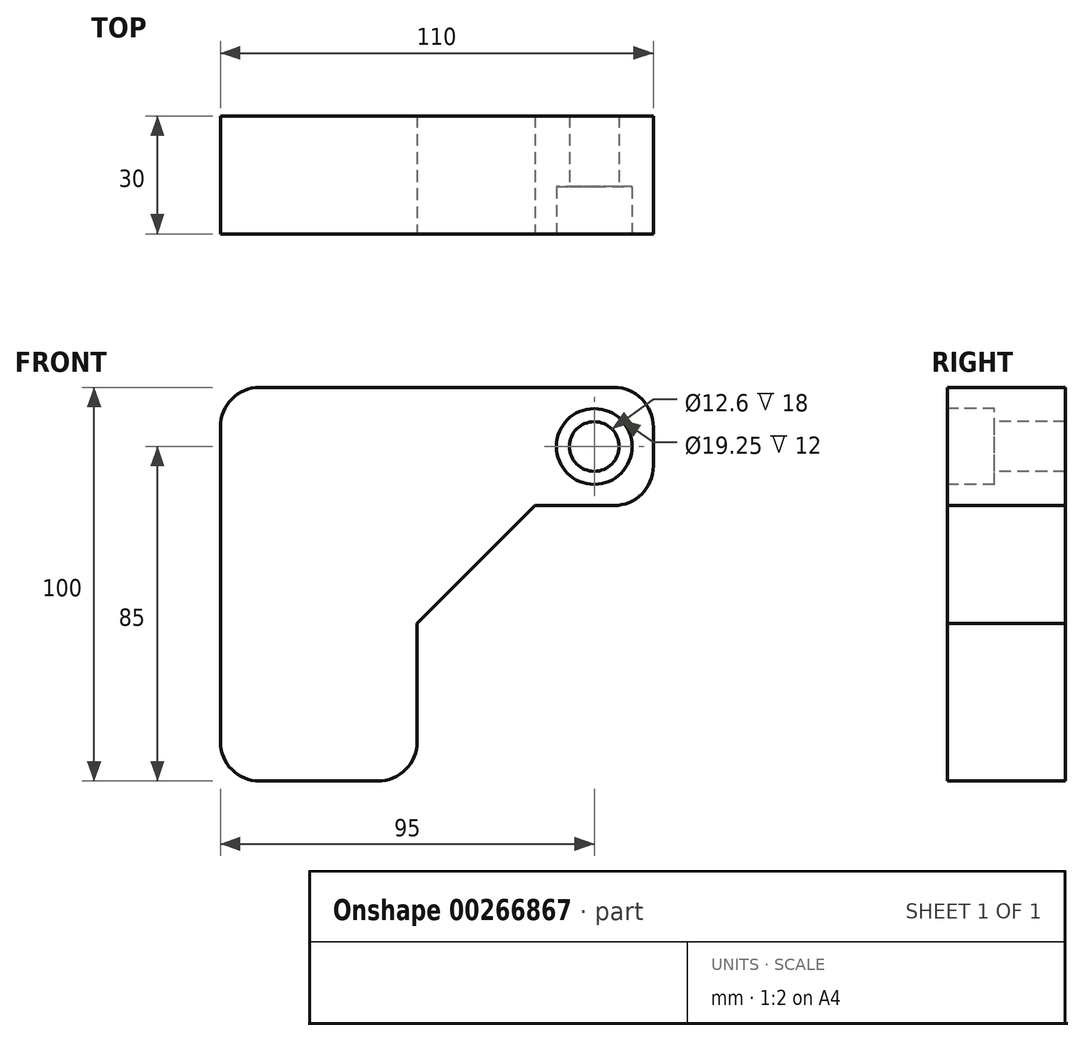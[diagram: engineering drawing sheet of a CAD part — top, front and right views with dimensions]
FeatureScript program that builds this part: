
annotation { "Feature Type Name" : "Feature", "Feature Type Description" : "" }
export const myFeature = defineFeature(function(context is Context, id is Id, definition is map)
    precondition{}
    {
        {
            var Q0;
            Q0=qCreatedBy(makeId("Front.planeOp"),FACE);
            var sketch = newSketch(context, id + "F0", { "sketchPlane" : qUnion([Q0])});
            skLineSegment(sketch, "E0", {"start": v(0, 0) * mm, "end": v(30, 30) * mm});
            skLineSegment(sketch, "E1", {"start": v(60, 60) * mm, "end": v(-50, 60) * mm});
            skLineSegment(sketch, "E2", {"start": v(-50, 60) * mm, "end": v(-50, -40) * mm});
            skLineSegment(sketch, "E3", {"start": v(-50, -40) * mm, "end": v(0, -40) * mm});
            skLineSegment(sketch, "E4", {"start": v(0, -40) * mm, "end": v(0, 0) * mm});
            skLineSegment(sketch, "E5", {"start": v(30, 30) * mm, "end": v(60, 30) * mm});
            skLineSegment(sketch, "E6", {"start": v(60, 30) * mm, "end": v(60, 60) * mm});
            skPoint(sketch, "E7", {"position": v(45, 45) * mm});
            skLineSegment(sketch, "E8", {"start": v(-25, -40) * mm, "end": v(-25, 60) * mm, "construction": true});
            skSolve(sketch);
        }
        {
            var Q0;
            Q0 = qSketchRegion(id + "F0", true);
            extrude(context, id + "F1", {"entities" : qUnion([Q0]), "oppositeDirection" : true, "depth" : 30 * mm});
        }
        {
            var Q0;
            Q0=makeQuery(id+"F1.opExtrude","SWEPT_EDGE",EDGE,{"disambiguationData":[OSD([sQuery(id+"F0.wireOp",EDGE,"E2"),sQuery(id+"F0.wireOp",EDGE,"E3")])]});
            var Q1;
            Q1=makeQuery(id+"F1.opExtrude","SWEPT_EDGE",EDGE,{"disambiguationData":[OSD([sQuery(id+"F0.wireOp",EDGE,"E3"),sQuery(id+"F0.wireOp",EDGE,"E4")])]});
            var Q2;
            Q2=makeQuery(id+"F1.opExtrude","SWEPT_EDGE",EDGE,{"disambiguationData":[OSD([sQuery(id+"F0.wireOp",EDGE,"E1"),sQuery(id+"F0.wireOp",EDGE,"E2")])]});
            var Q3;
            Q3=makeQuery(id+"F1.opExtrude","SWEPT_EDGE",EDGE,{"disambiguationData":[OSD([sQuery(id+"F0.wireOp",EDGE,"E1"),sQuery(id+"F0.wireOp",EDGE,"E6")])]});
            var Q4;
            Q4=makeQuery(id+"F1.opExtrude","SWEPT_EDGE",EDGE,{"disambiguationData":[OSD([sQuery(id+"F0.wireOp",EDGE,"E5"),sQuery(id+"F0.wireOp",EDGE,"E6")])]});
            fillet(context, id + "F2", {"entities" : qUnion([Q0, Q1, Q2, Q3, Q4]), "radius" : 10 * mm, "tangentPropagation" : true, "allowEdgeOverflow" : false});
        }
        {
            var Q0;
            Q0=sQuery(id+"F0.wireOp",VERTEX,"E7");
            var Q1;
            Q1=makeQuery(id+"F1.opExtrude","SWEPT_BODY",BODY,{"disambiguationData":[OSD([sQuery(id+"F0.wireOp",EDGE,"E0"),sQuery(id+"F0.wireOp",EDGE,"E1"),sQuery(id+"F0.wireOp",EDGE,"E2"),sQuery(id+"F0.wireOp",EDGE,"E3"),sQuery(id+"F0.wireOp",EDGE,"E4"),sQuery(id+"F0.wireOp",EDGE,"E5"),sQuery(id+"F0.wireOp",EDGE,"E6")])]});
            hole(context, id + "F3", {"style" : HoleStyle.C_BORE, "endStyle" : HoleEndStyle.THROUGH, "standardTappedOrClearance" : lookupTablePath({ "standard" : "ISO", "fit" : "Close", "size" : "M12", "type" : "Clearance" }), "standardBlindInLast" : lookupTablePath({ "fit" : "Close", "standard" : "ISO", "size" : "M12", "type" : "Clearance" }), "holeDiameter" : 12.6 * mm, "cBoreDiameter" : 19.25 * mm, "cBoreDepth" : 12 * mm, "tappedDepth" : 12 * mm, "tapClearance" : 3, "locations" : qUnion([Q0]), "scope" : qUnion([Q1])});
        }
    });
